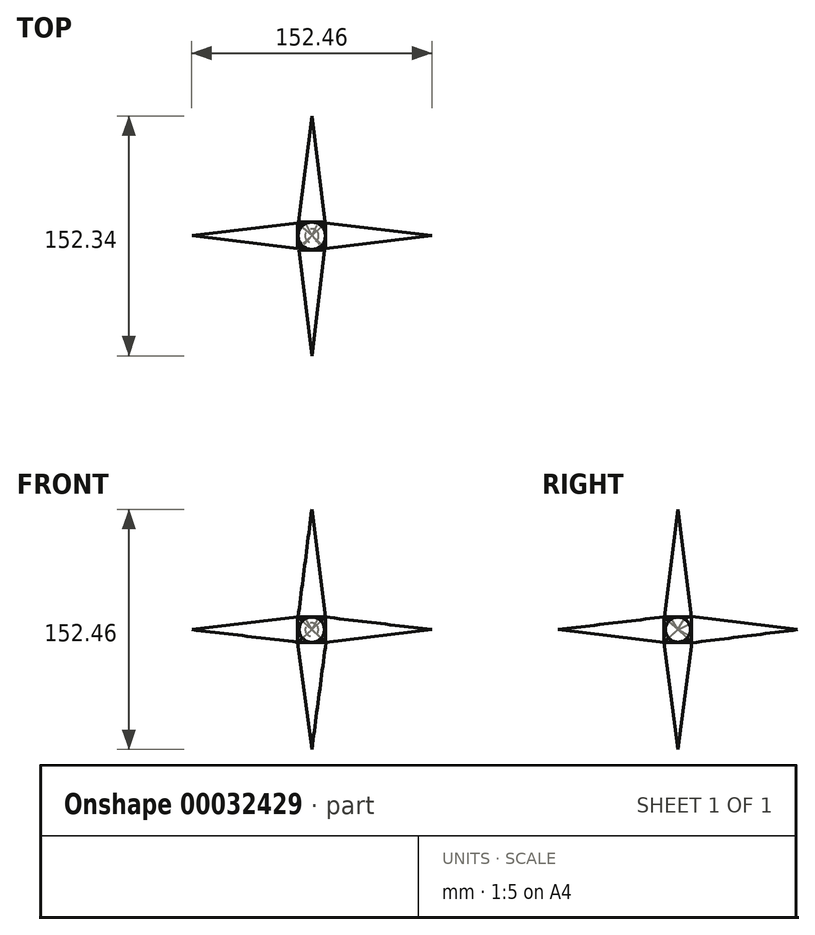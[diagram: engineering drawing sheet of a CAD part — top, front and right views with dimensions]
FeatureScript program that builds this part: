
annotation { "Feature Type Name" : "Feature", "Feature Type Description" : "" }
export const myFeature = defineFeature(function(context is Context, id is Id, definition is map)
    precondition{}
    {
        {
            var Q0;
            Q0=qCreatedBy(makeId("Front.planeOp"),FACE);
            var sketch = newSketch(context, id + "F0", { "sketchPlane" : qUnion([Q0])});
            skLineSegment(sketch, "E0", {"start": v(-8.69, 7.99) * mm, "end": v(0, 76.37) * mm});
            skLineSegment(sketch, "E1", {"start": v(0, 76.37) * mm, "end": v(0, 0) * mm});
            skLineSegment(sketch, "E2", {"start": v(-8.69, 7.99) * mm, "end": v(-4.34, 7.44) * mm});
            skPoint(sketch, "E2.endSnap0", {"position": v(-4.34, 4) * mm});
            skLineSegment(sketch, "E3", {"start": v(-4.34, 7.44) * mm, "end": v(0, 0) * mm});
            skSolve(sketch);
        }
        {
            var Q0;
            Q0 = qSketchRegion(id + "F0", true);
            var Q1;
            Q1=sQuery(id+"F0.wireOp",EDGE,"E1");
            revolve(context, id + "F1", {"entities" : qUnion([Q0]), "axis" : qUnion([Q1]), "revolveType" : RevolveType.FULL});
        }
        {
            var Q0;
            Q0=qCreatedBy(makeId("Front.planeOp"),FACE);
            var sketch = newSketch(context, id + "F2", { "sketchPlane" : qUnion([Q0])});
            skLineSegment(sketch, "E4", {"start": v(0, 0) * mm, "end": v(-76.23, 0) * mm});
            skLineSegment(sketch, "E5", {"start": v(-76.23, 0) * mm, "end": v(-8.97, 7.99) * mm});
            skLineSegment(sketch, "E6", {"start": v(-8.97, 7.99) * mm, "end": v(0, 0) * mm});
            skSolve(sketch);
        }
        {
            var Q0;
            Q0 = qSketchRegion(id + "F2", true);
            var Q1;
            Q1=sQuery(id+"F2.wireOp",EDGE,"E4");
            revolve(context, id + "F3", {"entities" : qUnion([Q0]), "axis" : qUnion([Q1]), "revolveType" : RevolveType.FULL});
        }
        {
            var Q0;
            Q0=qCreatedBy(makeId("Front.planeOp"),FACE);
            var sketch = newSketch(context, id + "F4", { "sketchPlane" : qUnion([Q0])});
            skLineSegment(sketch, "E7", {"start": v(0, 0) * mm, "end": v(-8.97, -8.27) * mm});
            skLineSegment(sketch, "E8", {"start": v(-8.97, -8.27) * mm, "end": v(0, -76.09) * mm});
            skLineSegment(sketch, "E9", {"start": v(0, -76.09) * mm, "end": v(0, 0) * mm});
            skSolve(sketch);
        }
        {
            var Q0;
            Q0 = qSketchRegion(id + "F4", true);
            var Q1;
            Q1=sQuery(id+"F4.wireOp",EDGE,"E9");
            revolve(context, id + "F5", {"entities" : qUnion([Q0]), "axis" : qUnion([Q1]), "revolveType" : RevolveType.FULL});
        }
        {
            var Q0;
            Q0=qCreatedBy(makeId("Front.planeOp"),FACE);
            var sketch = newSketch(context, id + "F6", { "sketchPlane" : qUnion([Q0])});
            skLineSegment(sketch, "E10", {"start": v(8.69, 7.99) * mm, "end": v(76.23, 0) * mm});
            skLineSegment(sketch, "E11", {"start": v(76.23, 0) * mm, "end": v(0, 0) * mm});
            skLineSegment(sketch, "E12", {"start": v(0, 0) * mm, "end": v(8.69, 7.99) * mm});
            skSolve(sketch);
        }
        {
            var Q0;
            Q0=makeQuery(id+"F6.imprint","IMPRINT",FACE,{"disambiguationData":[TD([[makeQuery(id+"F6.imprint","IMPRINT",EDGE,{"derivedFrom":sQuery(id+"F6.wireOp",EDGE,"E10")}),-1.0]])]});
            var Q1;
            Q1=sQuery(id+"F6.wireOp",EDGE,"E11");
            revolve(context, id + "F7", {"entities" : qUnion([Q0]), "axis" : qUnion([Q1]), "revolveType" : RevolveType.FULL});
        }
        {
            var Q0;
            Q0=qCreatedBy(makeId("Right.planeOp"),FACE);
            var sketch = newSketch(context, id + "F8", { "sketchPlane" : qUnion([Q0])});
            skLineSegment(sketch, "E13", {"start": v(0, 0) * mm, "end": v(-8.98, 8.08) * mm});
            skLineSegment(sketch, "E14", {"start": v(-8.98, 8.08) * mm, "end": v(-76.31, 0) * mm});
            skLineSegment(sketch, "E15", {"start": v(-76.31, 0) * mm, "end": v(0, 0) * mm});
            skSolve(sketch);
        }
        {
            var Q0;
            Q0=makeQuery(id+"F8.imprint","IMPRINT",FACE,{"disambiguationData":[TD([[makeQuery(id+"F8.imprint","IMPRINT",EDGE,{"derivedFrom":sQuery(id+"F8.wireOp",EDGE,"E13")}),1.0]])]});
            var Q1;
            Q1=sQuery(id+"F8.wireOp",EDGE,"E15");
            revolve(context, id + "F9", {"entities" : qUnion([Q0]), "axis" : qUnion([Q1]), "revolveType" : RevolveType.FULL});
        }
        {
            var Q0;
            Q0=qCreatedBy(makeId("Right.planeOp"),FACE);
            var sketch = newSketch(context, id + "F10", { "sketchPlane" : qUnion([Q0])});
            skLineSegment(sketch, "E16", {"start": v(8.7, 8.36) * mm, "end": v(76.03, 0) * mm});
            skLineSegment(sketch, "E17", {"start": v(76.03, 0) * mm, "end": v(0, 0) * mm});
            skLineSegment(sketch, "E18", {"start": v(0, 0) * mm, "end": v(8.7, 4.18) * mm});
            skPoint(sketch, "E18.endSnap0", {"position": v(4.35, 4.18) * mm});
            skLineSegment(sketch, "E19", {"start": v(8.7, 4.18) * mm, "end": v(8.7, 8.36) * mm});
            skSolve(sketch);
        }
        {
            var Q0;
            Q0 = qSketchRegion(id + "F10", true);
            var Q1;
            Q1=sQuery(id+"F10.wireOp",EDGE,"E17");
            revolve(context, id + "F11", {"entities" : qUnion([Q0]), "axis" : qUnion([Q1]), "revolveType" : RevolveType.FULL});
        }
    });
